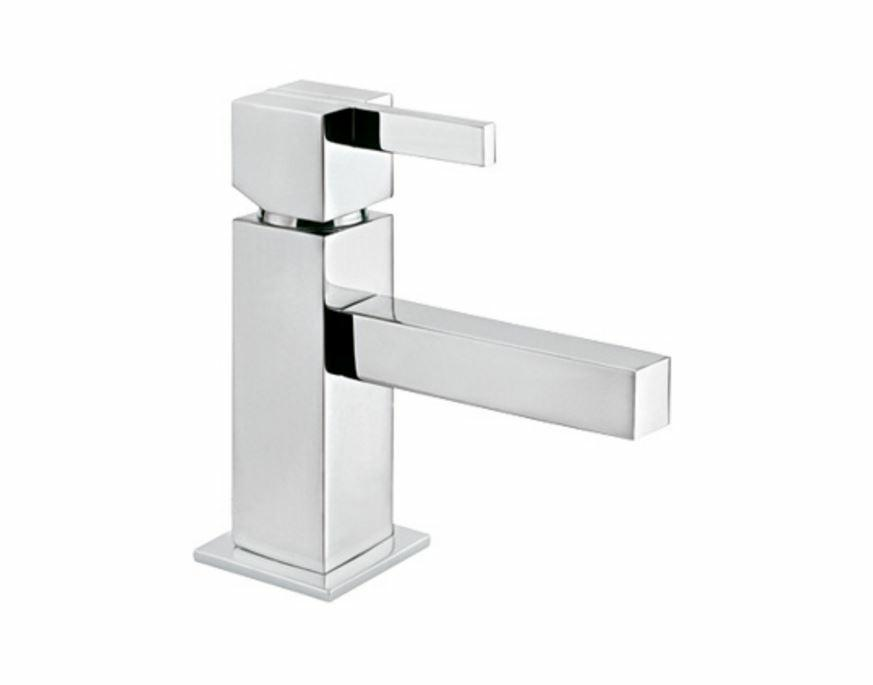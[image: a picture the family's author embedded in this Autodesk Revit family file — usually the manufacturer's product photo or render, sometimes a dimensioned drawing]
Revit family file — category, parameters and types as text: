
# Revit family: Monomando de Lavabo EP-94
name_source: partatom
category: Aparatos sanitarios
revit_build: Autodesk Revit 2016 (Build: 20150220_1215(x64)
units: mm (PartAtom-declared; Revit-internal decimal feet)

## family parameters
Compartido = Sí
Corte con vacíos al cargar = No
Cota de conector redondo = Diámetro de uso
Número OmniClass = 23.45.55.14
Punto de cálculo de habitación = Sí
Se basa en plano de trabajo = Sí
Siempre vertical = Sí
Tipo de pieza = Normal
Título OmniClass = Single Faucets

## types (1)
- EP-94
    Brass Chromed = Brass
    Comentarios de tipo = Single Control Lavatory Faucet
    Data Sheet = http://www.helvex.com.mx
    Descripción = Kúbica Single Control With Push Drain
    Elevación por defecto = 1"
    Fabricante = HELVEX
    Features = Single Control Ceramic Cartridge; Setting Tool Includes; Flexible Hoses 12" Length; Push Drain With Overflow
    Imagen de tipo = EP-94.JPG
    Inlet Threads = ½" - 14 NPSM
    Instructive = http://www.helvex.com.mx
    Max. Working Pressure = 85.3 psi
    Min. Working Pressure = 8.5 psi
    Modelo = EP-94
    Satin = Satín
    Total Height = 7"
    Total Length = 6"
    Total Width = 3"
    URL = http://www.helvex.com.mx

## geometry (parser evidence)
native form markers: Sweep x3
no freeform markers — native parametric forms only
